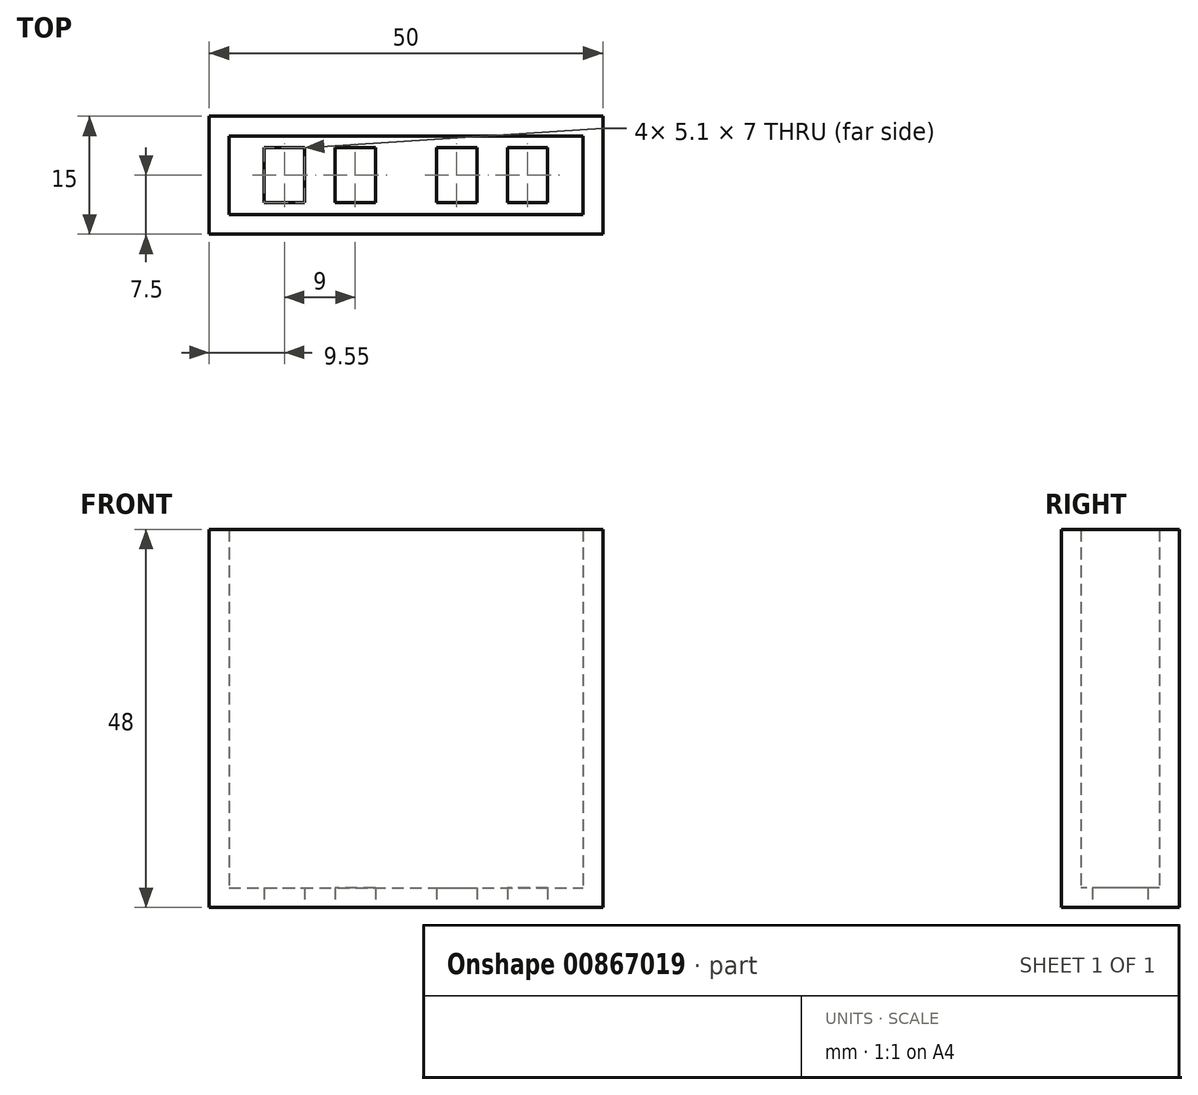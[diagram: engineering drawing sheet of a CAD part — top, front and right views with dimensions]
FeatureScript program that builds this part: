
annotation { "Feature Type Name" : "Feature", "Feature Type Description" : "" }
export const myFeature = defineFeature(function(context is Context, id is Id, definition is map)
    precondition{}
    {
        {
            var Q0;
            Q0=qCreatedBy(makeId("Top.planeOp"),FACE);
            var sketch = newSketch(context, id + "F0", { "sketchPlane" : qUnion([Q0])});
            skLineSegment(sketch, "E0.bottom", {"start": v(-25, 7.5) * mm, "end": v(25, 7.5) * mm});
            skLineSegment(sketch, "E0.top", {"start": v(-25, -7.5) * mm, "end": v(25, -7.5) * mm});
            skLineSegment(sketch, "E0.left", {"start": v(-25, 7.5) * mm, "end": v(-25, -7.5) * mm});
            skLineSegment(sketch, "E0.right", {"start": v(25, 7.5) * mm, "end": v(25, -7.5) * mm});
            skPoint(sketch, "E0.middle", {"position": v(0, 0) * mm});
            skLineSegment(sketch, "E1.bottom", {"start": v(-3.9, 3.5) * mm, "end": v(-9, 3.5) * mm});
            skLineSegment(sketch, "E1.top", {"start": v(-3.9, -3.5) * mm, "end": v(-9, -3.5) * mm});
            skLineSegment(sketch, "E1.left", {"start": v(-3.9, 3.5) * mm, "end": v(-3.9, -3.5) * mm});
            skLineSegment(sketch, "E1.right", {"start": v(-9, 3.5) * mm, "end": v(-9, -3.5) * mm});
            skPoint(sketch, "E1.middle", {"position": v(-6.45, 0) * mm});
            skLineSegment(sketch, "E2.bottom", {"start": v(-18, 3.5) * mm, "end": v(-12.9, 3.5) * mm});
            skLineSegment(sketch, "E2.top", {"start": v(-18, -3.5) * mm, "end": v(-12.9, -3.5) * mm});
            skLineSegment(sketch, "E2.left", {"start": v(-18, 3.5) * mm, "end": v(-18, -3.5) * mm});
            skLineSegment(sketch, "E2.right", {"start": v(-12.9, 3.5) * mm, "end": v(-12.9, -3.5) * mm});
            skPoint(sketch, "E2.middle", {"position": v(-15.45, 0) * mm});
            skLineSegment(sketch, "E3.MirrorCS", {"start": v(3.9, 3.5) * mm, "end": v(3.9, -3.5) * mm});
            skLineSegment(sketch, "E4.MirrorCS", {"start": v(3.9, -3.5) * mm, "end": v(9, -3.5) * mm});
            skLineSegment(sketch, "E5.MirrorCS", {"start": v(12.9, 3.5) * mm, "end": v(12.9, -3.5) * mm});
            skPoint(sketch, "E6.MirrorP", {"position": v(15.45, 0) * mm});
            skLineSegment(sketch, "E7.MirrorCS", {"start": v(3.9, 3.5) * mm, "end": v(9, 3.5) * mm});
            skLineSegment(sketch, "E8.MirrorCS", {"start": v(18, 3.5) * mm, "end": v(18, -3.5) * mm});
            skLineSegment(sketch, "E9.MirrorCS", {"start": v(9, 3.5) * mm, "end": v(9, -3.5) * mm});
            skLineSegment(sketch, "E10.MirrorCS", {"start": v(18, -3.5) * mm, "end": v(12.9, -3.5) * mm});
            skPoint(sketch, "E11.MirrorP", {"position": v(6.45, 0) * mm});
            skLineSegment(sketch, "E12.MirrorCS", {"start": v(18, 3.5) * mm, "end": v(12.9, 3.5) * mm});
            skSolve(sketch);
        }
        {
            var Q0;
            Q0 = qSketchRegion(id + "F0", true);
            extrude(context, id + "F1", {"entities" : qUnion([Q0]), "depth" : 48 * mm, "offsetDistance" : 25 * mm});
        }
        {
            var Q0;
            Q0=makeQuery(id+"F1.opExtrude","CAP_FACE",FACE,{"disambiguationData":[OSD([sQuery(id+"F0.wireOp",EDGE,"E0.bottom"),sQuery(id+"F0.wireOp",EDGE,"E0.top"),sQuery(id+"F0.wireOp",EDGE,"E0.left"),sQuery(id+"F0.wireOp",EDGE,"E0.right"),sQuery(id+"F0.wireOp",EDGE,"E1.bottom"),sQuery(id+"F0.wireOp",EDGE,"E1.top"),sQuery(id+"F0.wireOp",EDGE,"E1.left"),sQuery(id+"F0.wireOp",EDGE,"E1.right"),sQuery(id+"F0.wireOp",EDGE,"E2.bottom"),sQuery(id+"F0.wireOp",EDGE,"E2.top"),sQuery(id+"F0.wireOp",EDGE,"E2.left"),sQuery(id+"F0.wireOp",EDGE,"E2.right"),sQuery(id+"F0.wireOp",EDGE,"E3.MirrorCS"),sQuery(id+"F0.wireOp",EDGE,"E4.MirrorCS"),sQuery(id+"F0.wireOp",EDGE,"E5.MirrorCS"),sQuery(id+"F0.wireOp",EDGE,"E7.MirrorCS"),sQuery(id+"F0.wireOp",EDGE,"E8.MirrorCS"),sQuery(id+"F0.wireOp",EDGE,"E9.MirrorCS"),sQuery(id+"F0.wireOp",EDGE,"E10.MirrorCS"),sQuery(id+"F0.wireOp",EDGE,"E12.MirrorCS")])],"isStart":false});
            var Q1;
            Q1=makeQuery(id+"F1.opExtrude","SWEPT_FACE",FACE,{"disambiguationData":[OSD([sQuery(id+"F0.wireOp",EDGE,"E1.right")])]});
            var Q2;
            Q2=makeQuery(id+"F1.opExtrude","SWEPT_FACE",FACE,{"disambiguationData":[OSD([sQuery(id+"F0.wireOp",EDGE,"E1.left")])]});
            var Q3;
            Q3=makeQuery(id+"F1.opExtrude","SWEPT_FACE",FACE,{"disambiguationData":[OSD([sQuery(id+"F0.wireOp",EDGE,"E1.top")])]});
            var Q4;
            Q4=makeQuery(id+"F1.opExtrude","SWEPT_FACE",FACE,{"disambiguationData":[OSD([sQuery(id+"F0.wireOp",EDGE,"E2.top")])]});
            var Q5;
            Q5=makeQuery(id+"F1.opExtrude","SWEPT_FACE",FACE,{"disambiguationData":[OSD([sQuery(id+"F0.wireOp",EDGE,"E4.MirrorCS")])]});
            var Q6;
            Q6=makeQuery(id+"F1.opExtrude","SWEPT_FACE",FACE,{"disambiguationData":[OSD([sQuery(id+"F0.wireOp",EDGE,"E10.MirrorCS")])]});
            var Q7;
            Q7=makeQuery(id+"F1.opExtrude","SWEPT_FACE",FACE,{"disambiguationData":[OSD([sQuery(id+"F0.wireOp",EDGE,"E5.MirrorCS")])]});
            var Q8;
            Q8=makeQuery(id+"F1.opExtrude","SWEPT_FACE",FACE,{"disambiguationData":[OSD([sQuery(id+"F0.wireOp",EDGE,"E3.MirrorCS")])]});
            var Q9;
            Q9=makeQuery(id+"F1.opExtrude","SWEPT_FACE",FACE,{"disambiguationData":[OSD([sQuery(id+"F0.wireOp",EDGE,"E2.left")])]});
            var Q10;
            Q10=makeQuery(id+"F1.opExtrude","SWEPT_FACE",FACE,{"disambiguationData":[OSD([sQuery(id+"F0.wireOp",EDGE,"E2.bottom")])]});
            var Q11;
            Q11=makeQuery(id+"F1.opExtrude","SWEPT_FACE",FACE,{"disambiguationData":[OSD([sQuery(id+"F0.wireOp",EDGE,"E1.bottom")])]});
            var Q12;
            Q12=makeQuery(id+"F1.opExtrude","SWEPT_FACE",FACE,{"disambiguationData":[OSD([sQuery(id+"F0.wireOp",EDGE,"E7.MirrorCS")])]});
            var Q13;
            Q13=makeQuery(id+"F1.opExtrude","SWEPT_FACE",FACE,{"disambiguationData":[OSD([sQuery(id+"F0.wireOp",EDGE,"E12.MirrorCS")])]});
            var Q14;
            Q14=makeQuery(id+"F1.opExtrude","SWEPT_FACE",FACE,{"disambiguationData":[OSD([sQuery(id+"F0.wireOp",EDGE,"E8.MirrorCS")])]});
            var Q15;
            Q15=makeQuery(id+"F1.opExtrude","SWEPT_FACE",FACE,{"disambiguationData":[OSD([sQuery(id+"F0.wireOp",EDGE,"E9.MirrorCS")])]});
            var Q16;
            Q16=makeQuery(id+"F1.opExtrude","SWEPT_FACE",FACE,{"disambiguationData":[OSD([sQuery(id+"F0.wireOp",EDGE,"E2.right")])]});
            shell(context, id + "F2", {"entities" : qUnion([Q0, Q1, Q2, Q3, Q4, Q5, Q6, Q7, Q8, Q9, Q10, Q11, Q12, Q13, Q14, Q15, Q16]), "thickness" : 2.5 * mm});
        }
    });
